# Revit family: PRESTO XT-I
name_source: partatom
category: Aparatos sanitarios
revit_build: Autodesk Revit 2015 (Build: 20140223_1515(x64)
units: mm (PartAtom-declared; Revit-internal decimal feet)

## types (1)
- 14209
    Accionamiento = Por pulsador
    CAUDAL = 1.5 L/Min
    CIERRE = Automático en 7 seg.
    Comentarios de tipo = ◦Cabeza intercambiable que comprende todo el mecanismo del grifo
◦Cuerpo y pulsador en latón cromado, piezas interiores en materiales resistentes a la corrosión y a las incrustaciones calcáreas
◦Suministro con arandela, tuerca racor de salida y junta americana para tubo de Ø 28 mm.
    Conexión AC = Sí
    Conexión AF = Sí
    Código de montaje = C1030220
    Descripción = Fluxor temporizado de fijación sobre muro con cuerpo y embellecedor en latón cromado. Dispositivo antiSifónico incorporado. Pistón intercambiable.
    ENTRADA = Macho 3/4"
    Elevación por defecto = 1219 mm
    Fabricante = PRESTO IBÉRICA
    Imagen de tipo = <Ninguno>
    Material = LATON CROMADO
    Modelo = PRESTO XT I
    PESO BRUTO = 0.790 Kg
    REFERENCIA = 14209
    TIPO DE AGUA = Fria
    Teléfono = (+34) 915 782 575
    URL = http://www.prestoiberica.com
